# Revit family: DC_Rheem_PLM_Raypak_B1852HWT
name_source: partatom
category: Plumbing Fixtures
revit_build: Autodesk Revit 2017 (Build: 20160225_1515(x64)
units: mm (PartAtom-declared; Revit-internal decimal feet)

## family parameters
Cut with Voids When Loaded = No
Host = Face
Part Type = Normal
Room Calculation Point = No
Round Connector Dimension = Use Radius
Shared = No

## types (4) — shared parameters
BaseDist_ANZRS = 60 mm
BaseHeight_ANZRS = 45 mm  [stored 0.147638 ft]
BaseWidth_ANZRS = 50 mm  [stored 0.164042 ft]
BoxHeight_ANZRS = 930 mm  [stored 3.05118 ft]
ColdWaterPipeDiameter_ANZRS = 65 mm  [stored 0.213255 ft]
ColdWaterPipeDisi_ANZRS = 280 mm  [stored 0.918635 ft]
ColdWaterPipeRadius_ANZRS = 33 mm
ConnHeight_ANZRS = 755 mm
EleBoxHeight_ANZRS = 380 mm  [stored 1.24672 ft]
EleBoxHeightfromBase_ANZRS = 245 mm  [stored 0.803806 ft]
EleBoxWidth_ANZRS = 160 mm
GasPipeDist_ANZRS = 130 mm
GasPipeHeight_ANZRS = 410 mm  [stored 1.34514 ft]
Height_ANZRS = 2920 mm
HotWaterPipeDiameter_ANZRS = 65 mm  [stored 0.213255 ft]
HotWaterPipeDist_ANZRS = 155 mm  [stored 0.50853 ft]
HotWaterPipeRadius_ANZRS = 33 mm
Length_ANZRS = 2270 mm
Manufacturer = Raypak
Materials_ANZRS = Raypak - Grey Powder Coated Steel
PVRDist_ANZRS = 85 mm  [stored 0.278871 ft]
TopBigDia_ANZRS = 700 mm
TopH1_ANZRS = 300 mm
TopH2_ANZRS = 480 mm  [stored 1.5748 ft]
TopSmallDia_ANZRS = 505 mm  [stored 1.65682 ft]
URL = http://www.rheem.com.au
zero-valued in all types: Default Elevation

## per-type parameters (varying)
| type | GasPipeDiameter_ANZRS | GasPipeRadius_ANZRS | Model | PRVDiameter_ANZRS | PRVRadius_ANZRS | Type Comments |
| Raypak - Gas Water Heater- Outdoor - 1854 MJ/h  Natural gas, modulating gas control | 50 mm  [stored 0.164042 ft] | 25 mm  [stored 0.082021 ft] | B1852NCM/HWT | 20 mm  [stored 0.0656168 ft] | 10 mm  [stored 0.0328084 ft] | Recovery 7052L/h @ 50°C rise |
| Raypak - Gas Water Heater- Outdoor - 1854 MJ/h  Natural gas, On/Off gas control | 50 mm  [stored 0.164042 ft] | 25 mm  [stored 0.082021 ft] | B1852NCO/HWT | 30 mm  [stored 0.0984252 ft] | 15 mm | Recovery 7052L/h @ 50°C rise |
| Raypak - Gas Water Heater- Outdoor - 1772 MJ/h  Propane gas, modulating gas control | 40 mm  [stored 0.131234 ft] | 20 mm  [stored 0.0656168 ft] | B1852PCM/HWT | 20 mm  [stored 0.0656168 ft] | 10 mm  [stored 0.0328084 ft] | Recovery 6794L/h @ 50°C rise |
| Raypak - Gas Water Heater- Outdoor - 1772 MJ/h  Propane gas, On/Off gas control | 40 mm  [stored 0.131234 ft] | 20 mm  [stored 0.0656168 ft] | B1852PCO/HWT | 20 mm  [stored 0.0656168 ft] | 10 mm  [stored 0.0328084 ft] | Recovery 6794L/h @ 50°C rise |

note: column(s) folded — value = type name in every type: Description

note: [stored X ft] marks values corroborated as IEEE doubles in the binary element streams (Revit-internal decimal feet)

## geometry (parser evidence)
native form markers: Blend x6, Sweep x2
no freeform markers — native parametric forms only
